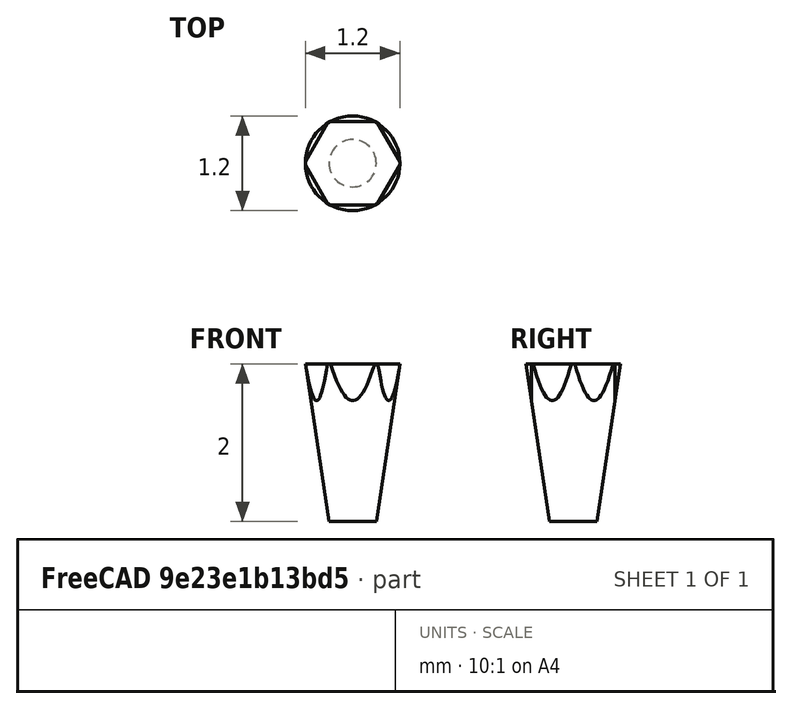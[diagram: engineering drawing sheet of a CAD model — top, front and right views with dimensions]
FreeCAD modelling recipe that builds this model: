
FCSTD DOCUMENT  (FreeCAD 0.16R6712 (Git))
Label: pencil2
License: All rights reserved
LicenseURL: http://en.wikipedia.org/wiki/All_rights_reserved
objects: Part::Cone×1, Sketcher::SketchObject×1, PartDesign::Pocket×1, PartDesign::PolarPattern×1, Mesh::Feature×1
note: 5 computed .brp shape members not serialized (recipe doc carries the construction recipe); baked Part::Feature solids carry a one-line shape summary decoded from their .brp

FEATURE [Part::Cone] Cone
  Angle = 360
  Height = 2
  Placement = pos=(0,0,-22) rot=(0,0,1;0rad)
  Radius1 = 0.3
  Radius2 = 0.6
FEATURE [Sketcher::SketchObject] Sketch
  Placement = pos=(0,0,-20) rot=(0,0,1;0rad)
  Support = -> Cone [Face2]
  sketch-geometry (4):
    g0: LineSegment StartX=-0.3 StartY=0.83 StartZ=0 EndX=0.3 EndY=0.83 EndZ=0
    g1: LineSegment StartX=0.3 StartY=0.83 StartZ=0 EndX=0.3 EndY=0.53 EndZ=0
    g2: LineSegment StartX=0.3 StartY=0.53 StartZ=0 EndX=-0.3 EndY=0.53 EndZ=0
    g3: LineSegment StartX=-0.3 StartY=0.53 StartZ=0 EndX=-0.3 EndY=0.83 EndZ=0
  constraints (12):
    c: Coincident(g0,g1)
    c: Coincident(g1,g2)
    c: Coincident(g2,g3)
    c: Coincident(g3,g0)
    c: Horizontal(g0)
    c: Horizontal(g2)
    c: Vertical(g1)
    c: Vertical(g3)
    c: Symmetric(g0,g0,g-2)
    c: DistanceY(g-1,g1) = 0.53
    c: DistanceX(g-2,g1) = 0.3
    c: DistanceY(g2,g0) = 0.3
FEATURE [PartDesign::Pocket] Pocket
  Length = 10
  Placement = pos=(0,0,-22) rot=(0,0,1;0rad)
  Sketch = -> Sketch
  Type = 0
FEATURE [PartDesign::PolarPattern] PolarPattern
  Angle = 360
  Axis = -> Sketch [N_Axis]
  Occurrences = 6
  Originals = -> [Pocket]
  Placement = pos=(0,0,-22) rot=(0,0,1;0rad)
FEATURE [Mesh::Feature] Mesh  label="PolarPattern (Meshed)"
